# Revit family: Kawneer - AA3200 HP-Sub Sash OX
name_source: partatom
category: Doors
revit_build: Autodesk Revit 2015 (Build: 20140905_0730(x64)
units: mm (PartAtom-declared; Revit-internal decimal feet)

## types (1)
- AA3200 HP-Sub Sash OX
    2-Clolor Option = yes
    Air Infiltration (ASTM E 283) = < 0.30 cfm/ft2  @ 6.24 psf (300 Pa)
    Application = Low-rise, medium-rise, high-rise
    Assembly Code = B2030110
    CRF = 49 frame 57 glass (clear)
    CSI Masterformat Code = 08 32 13
    Cofigurations = OX, XO, OOX, XOO, OXO, OXXO
    Color = Anodize or Paint
    Condensation Index "I" = 39 (Clear Low-E)
    Description = Sliding Door, designed to meet thermal, coastal and hurricane resistant conditions, helps meet these challenges. Available in both High Performance (HP) and Hurricane Resistant (IR) versions, AA®3200 ISOWEB® Sliding Door complements Kawneer’s portfolio of thermal solutions and products for the entire building.  Kawneer’s high-performance ISOWEB® thermal break allows this slider to meet current energy codes and provides capabilities for a dual finished product. In addition to thermal performance, AA®3200 ISOWEB® Sliding Door has been tested for both large and small missile impact on panels up to 10' tall. For enhanced STC and OITC (sound resistance) performance, the slider accommodates 1-5/16" (33.3) insulated/ laminated glass, and it accommodates 1" (25.4) insulated glass for improved thermal performance.
    Design Pressure = AW-PG135-SD
    Door Corner Construction = Screw spline
    Door Panel Height = 6' - 10 1/2"
    Door Panel Width = 3' - 0 1/2"
    Frame Material = Aluminum - 6063-T6 alloy and temper
    Function = Interior
    Function (Interior or Exterior) = Exterior
    Glass Capture = Captured
    Glass Installation = inside or Pre-glaze
    Glazing Thickness = 0' - 0 1/2"
    Height = 7' - 0"
    Huricane Resistant Testing = Available - see AA3200 IR models
    Keywords = Entrance Door, Sliding Door, Condominium Door, High Performance, Impact Resistant, Hurricane Resistant
    Manufacturer = Kawneer
    Manufacturer Part Number = AA3200 HP-Sub Sash (OX)
    Model = OX
    Operating force (to Open) = < 40lbf
    Operating force (to keep motion) = < 25 lbf
    Overall U-Factor = 0.45 to 0.63
    Panel Inserts Material = Glass
    Product data url = https://bimobject.com
    Short Description = AA3200 ISOWEB Sliding Door
    Sightline = 0' - 0"
    Thickness = 0' - 0"
    Type Comments = Thermal Sliding Door
    Type of Glazing = Insulating
    URL = http://www.kawneer.com
    Wall Closure = By host
    Water - Static (ASTM E 331) = 15 psf
    Width = 6' - 0"

## geometry (parser evidence)
native form markers: Extrusion x5, Sweep x12
no freeform markers — native parametric forms only
